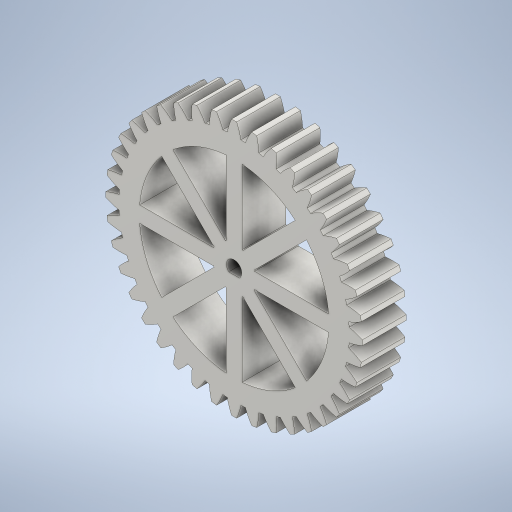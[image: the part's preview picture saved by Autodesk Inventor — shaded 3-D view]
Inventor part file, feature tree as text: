
AUTODESK INVENTOR PART (.ipt)
format: ipt  version: 2023 (Build 270158000, 158)  size: 562,688 bytes
history: native  units: mm (DEFAULTED — no unit token found)
features: sketch x4, extrude x3, plane x3, other x3
ambient origin geometry x8: Origin, YZ Plane, XZ Plane, XY Plane, X Axis, Y Axis, Z Axis, Center Point
bodies: Solid1 (feature_tree)
feature tree (13):
  extrude  "Extrusion1"  Depth=15.0mm TaperAngle=0.0deg
  plane  "Work Plane2"
  plane  "Work Plane8"
  plane  "Work Plane9"
  other  "Spur Gear"
  extrude  "Extrusion2"  Depth=10.0mm TaperAngle=0.0deg
  extrude  "Extrusion3"  Depth=0.785398mm TaperAngle=0.0deg
  sketch  "Sketch1"  dims[d0=88.0mm d1=15.0mm d2=0.0mm]
  sketch  "Sketch2"  dims[d3=80.0mm d4=10.0mm d5=0.0mm]
  other  "Srf1"
  sketch  "Sketch3"  dims[d16=200.0mm d17=0.0mm d34=0.785398mm]
  sketch  "Sketch4"  dims[d39=0.0mm d41=0.0mm d43=200.0mm d46=200.0mm d47=0.0mm d48=0.0mm d50=150.0mm d51=50.0mm d52=5.25mm d53=4.5mm d54=360.0deg d55=15.0mm d56=0.0mm d57=65.0mm d59=15.0mm d60=80.0mm d62=360.0deg d64=15.0mm d65=0.0mm]
  other  "Pitch Diameter"
